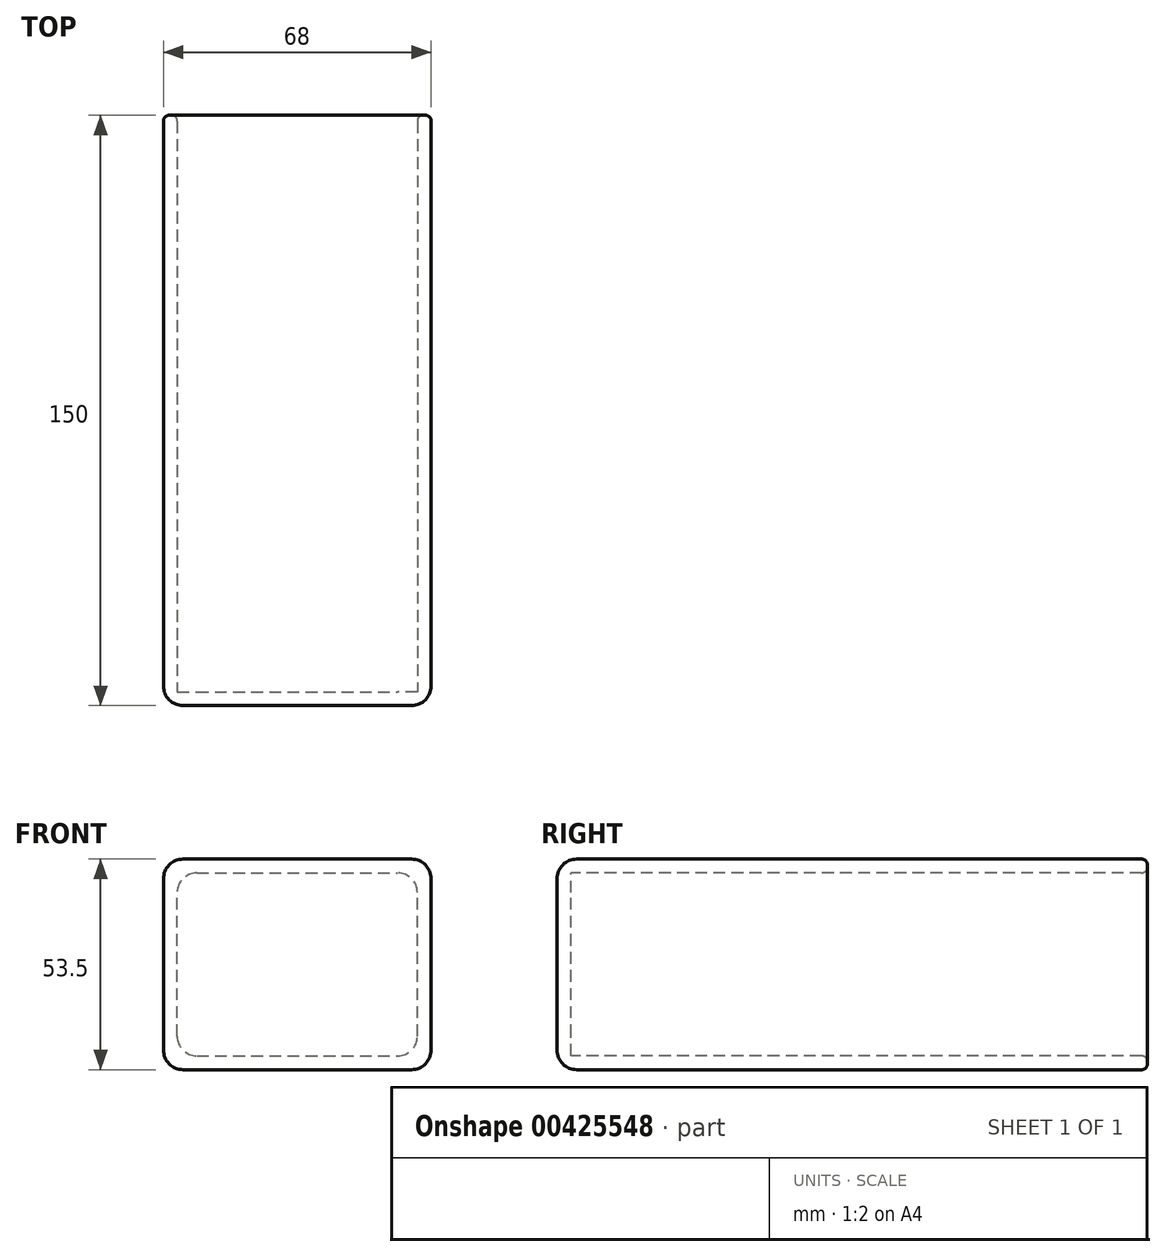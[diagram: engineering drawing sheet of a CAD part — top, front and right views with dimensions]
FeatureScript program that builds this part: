
annotation { "Feature Type Name" : "Feature", "Feature Type Description" : "" }
export const myFeature = defineFeature(function(context is Context, id is Id, definition is map)
    precondition{}
    {
        {
            var Q0;
            Q0=qCreatedBy(makeId("Front.planeOp"),FACE);
            var sketch = newSketch(context, id + "F0", { "sketchPlane" : qUnion([Q0])});
            skLineSegment(sketch, "E0.bottom", {"start": v(5, 0) * mm, "end": v(63, 0) * mm});
            skLineSegment(sketch, "E0.top", {"start": v(5, 53.5) * mm, "end": v(63, 53.5) * mm});
            skLineSegment(sketch, "E0.left", {"start": v(0, 5) * mm, "end": v(0, 48.5) * mm});
            skLineSegment(sketch, "E0.right", {"start": v(68, 5) * mm, "end": v(68, 48.5) * mm});
            skLineSegment(sketch, "E1.bottom", {"start": v(8.5, 3.5) * mm, "end": v(59.5, 3.5) * mm});
            skLineSegment(sketch, "E1.top", {"start": v(8.5, 50) * mm, "end": v(59.5, 50) * mm});
            skLineSegment(sketch, "E1.left", {"start": v(3.5, 8.5) * mm, "end": v(3.5, 45) * mm});
            skLineSegment(sketch, "E1.right", {"start": v(64.5, 8.5) * mm, "end": v(64.5, 45) * mm});
            skPoint(sketch, "E2.visualSharp", {"position": v(3.5, 50) * mm});
            skArc(sketch, "E2.filletArc", {"start": v(8.5, 50) * mm, "mid": v(4.96, 48.54) * mm, "end": v(3.5, 45) * mm});
            skPoint(sketch, "E3.visualSharp", {"position": v(0, 53.5) * mm});
            skArc(sketch, "E3.filletArc", {"start": v(5, 53.5) * mm, "mid": v(1.46, 52.04) * mm, "end": v(0, 48.5) * mm});
            skPoint(sketch, "E4.visualSharp", {"position": v(64.5, 50) * mm});
            skArc(sketch, "E4.filletArc", {"start": v(64.5, 45) * mm, "mid": v(63.04, 48.54) * mm, "end": v(59.5, 50) * mm});
            skPoint(sketch, "E5.visualSharp", {"position": v(68, 53.5) * mm});
            skArc(sketch, "E5.filletArc", {"start": v(68, 48.5) * mm, "mid": v(66.54, 52.04) * mm, "end": v(63, 53.5) * mm});
            skPoint(sketch, "E6.visualSharp", {"position": v(64.5, 3.5) * mm});
            skArc(sketch, "E6.filletArc", {"start": v(59.5, 3.5) * mm, "mid": v(63.04, 4.96) * mm, "end": v(64.5, 8.5) * mm});
            skPoint(sketch, "E7.visualSharp", {"position": v(68, 0) * mm});
            skArc(sketch, "E7.filletArc", {"start": v(63, 0) * mm, "mid": v(66.54, 1.46) * mm, "end": v(68, 5) * mm});
            skPoint(sketch, "E8.visualSharp", {"position": v(3.5, 3.5) * mm});
            skArc(sketch, "E8.filletArc", {"start": v(3.5, 8.5) * mm, "mid": v(4.96, 4.96) * mm, "end": v(8.5, 3.5) * mm});
            skPoint(sketch, "E9.visualSharp", {"position": v(0, 0) * mm});
            skArc(sketch, "E9.filletArc", {"start": v(0, 5) * mm, "mid": v(1.46, 1.46) * mm, "end": v(5, 0) * mm});
            skSolve(sketch);
        }
        {
            var Q0;
            Q0=makeQuery(id+"F0.imprint","IMPRINT",FACE,{"disambiguationData":[TD([[makeQuery(id+"F0.imprint","IMPRINT",EDGE,{"derivedFrom":sQuery(id+"F0.wireOp",EDGE,"E1.bottom")}),1.0]])]});
            extrude(context, id + "F1", {"entities" : qUnion([Q0]), "oppositeDirection" : true, "offsetDistance" : 25 * mm, "depth" : 3.5 * mm});
        }
        {
            var Q0;
            Q0=makeQuery(id+"F0.imprint","IMPRINT",FACE,{"disambiguationData":[TD([[makeQuery(id+"F0.imprint","IMPRINT",EDGE,{"derivedFrom":sQuery(id+"F0.wireOp",EDGE,"E0.bottom")}),1.0]])]});
            extrude(context, id + "F2", {"entities" : qUnion([Q0]), "operationType" : NewBodyOperationType.ADD, "oppositeDirection" : true, "offsetDistance" : 25 * mm, "depth" : 150 * mm});
        }
        {
            var Q0;
            Q0=makeQuery(id+"F2.opExtrude","CAP_EDGE",EDGE,{"disambiguationData":[OSD([sQuery(id+"F0.wireOp",EDGE,"E0.top")])],"isStart":true});
            var Q1;
            Q1=makeQuery(id+"F2.opExtrude","CAP_EDGE",EDGE,{"disambiguationData":[OSD([sQuery(id+"F0.wireOp",EDGE,"E3.filletArc")])],"isStart":true});
            var Q2;
            Q2=makeQuery(id+"F2.opExtrude","CAP_EDGE",EDGE,{"disambiguationData":[OSD([sQuery(id+"F0.wireOp",EDGE,"E0.left")])],"isStart":true});
            var Q3;
            Q3=makeQuery(id+"F2.opExtrude","CAP_EDGE",EDGE,{"disambiguationData":[OSD([sQuery(id+"F0.wireOp",EDGE,"E9.filletArc")])],"isStart":true});
            var Q4;
            Q4=makeQuery(id+"F2.opExtrude","CAP_EDGE",EDGE,{"disambiguationData":[OSD([sQuery(id+"F0.wireOp",EDGE,"E0.bottom")])],"isStart":true});
            var Q5;
            Q5=makeQuery(id+"F2.opExtrude","CAP_EDGE",EDGE,{"disambiguationData":[OSD([sQuery(id+"F0.wireOp",EDGE,"E7.filletArc")])],"isStart":true});
            var Q6;
            Q6=makeQuery(id+"F2.opExtrude","CAP_EDGE",EDGE,{"disambiguationData":[OSD([sQuery(id+"F0.wireOp",EDGE,"E0.right")])],"isStart":true});
            var Q7;
            Q7=makeQuery(id+"F2.opExtrude","CAP_EDGE",EDGE,{"disambiguationData":[OSD([sQuery(id+"F0.wireOp",EDGE,"E5.filletArc")])],"isStart":true});
            fillet(context, id + "F3", {"entities" : qUnion([Q0, Q1, Q2, Q3, Q4, Q5, Q6, Q7]), "radius" : 5 * mm, "tangentPropagation" : true, "allowEdgeOverflow" : false});
        }
        {
            var Q0;
            Q0=makeQuery(id+"F2.opExtrude","CAP_EDGE",EDGE,{"disambiguationData":[OSD([sQuery(id+"F0.wireOp",EDGE,"E0.top")])],"isStart":false});
            var Q1;
            Q1=makeQuery(id+"F2.opExtrude","CAP_EDGE",EDGE,{"disambiguationData":[OSD([sQuery(id+"F0.wireOp",EDGE,"E1.top")])],"isStart":false});
            var Q2;
            Q2=makeQuery(id+"F2.opExtrude","CAP_EDGE",EDGE,{"disambiguationData":[OSD([sQuery(id+"F0.wireOp",EDGE,"E3.filletArc")])],"isStart":false});
            var Q3;
            Q3=makeQuery(id+"F2.opExtrude","CAP_EDGE",EDGE,{"disambiguationData":[OSD([sQuery(id+"F0.wireOp",EDGE,"E2.filletArc")])],"isStart":false});
            var Q4;
            Q4=makeQuery(id+"F2.opExtrude","CAP_EDGE",EDGE,{"disambiguationData":[OSD([sQuery(id+"F0.wireOp",EDGE,"E0.left")])],"isStart":false});
            var Q5;
            Q5=makeQuery(id+"F2.opExtrude","CAP_EDGE",EDGE,{"disambiguationData":[OSD([sQuery(id+"F0.wireOp",EDGE,"E1.left")])],"isStart":false});
            var Q6;
            Q6=makeQuery(id+"F2.opExtrude","CAP_EDGE",EDGE,{"disambiguationData":[OSD([sQuery(id+"F0.wireOp",EDGE,"E9.filletArc")])],"isStart":false});
            var Q7;
            Q7=makeQuery(id+"F2.opExtrude","CAP_EDGE",EDGE,{"disambiguationData":[OSD([sQuery(id+"F0.wireOp",EDGE,"E8.filletArc")])],"isStart":false});
            var Q8;
            Q8=makeQuery(id+"F2.opExtrude","CAP_EDGE",EDGE,{"disambiguationData":[OSD([sQuery(id+"F0.wireOp",EDGE,"E1.bottom")])],"isStart":false});
            var Q9;
            Q9=makeQuery(id+"F2.opExtrude","CAP_EDGE",EDGE,{"disambiguationData":[OSD([sQuery(id+"F0.wireOp",EDGE,"E0.bottom")])],"isStart":false});
            var Q10;
            Q10=makeQuery(id+"F2.opExtrude","CAP_EDGE",EDGE,{"disambiguationData":[OSD([sQuery(id+"F0.wireOp",EDGE,"E7.filletArc")])],"isStart":false});
            var Q11;
            Q11=makeQuery(id+"F2.opExtrude","CAP_EDGE",EDGE,{"disambiguationData":[OSD([sQuery(id+"F0.wireOp",EDGE,"E6.filletArc")])],"isStart":false});
            var Q12;
            Q12=makeQuery(id+"F2.opExtrude","CAP_EDGE",EDGE,{"disambiguationData":[OSD([sQuery(id+"F0.wireOp",EDGE,"E0.right")])],"isStart":false});
            var Q13;
            Q13=makeQuery(id+"F2.opExtrude","CAP_EDGE",EDGE,{"disambiguationData":[OSD([sQuery(id+"F0.wireOp",EDGE,"E1.right")])],"isStart":false});
            var Q14;
            Q14=makeQuery(id+"F2.opExtrude","CAP_EDGE",EDGE,{"disambiguationData":[OSD([sQuery(id+"F0.wireOp",EDGE,"E4.filletArc")])],"isStart":false});
            var Q15;
            Q15=makeQuery(id+"F2.opExtrude","CAP_EDGE",EDGE,{"disambiguationData":[OSD([sQuery(id+"F0.wireOp",EDGE,"E5.filletArc")])],"isStart":false});
            fillet(context, id + "F4", {"entities" : qUnion([Q0, Q1, Q2, Q3, Q4, Q5, Q6, Q7, Q8, Q9, Q10, Q11, Q12, Q13, Q14, Q15]), "radius" : 1.5 * mm, "defaultsChanged" : true, "vertexSettings" : [], "allowEdgeOverflow" : false});
        }
    });
